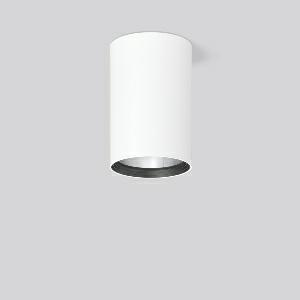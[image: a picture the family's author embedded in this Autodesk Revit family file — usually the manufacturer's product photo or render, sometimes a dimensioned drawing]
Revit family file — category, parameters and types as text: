
# Revit family: heledon_maxi_a_931223_002_1_76_c0e3
name_source: partatom
category: Lighting Fixtures
units: mm (PartAtom-declared; Revit-internal decimal feet)

## family parameters
Cut with Voids When Loaded = No
Host = Face
Light Source = No
Part Type = Normal
Room Calculation Point = No
Round Connector Dimension = Use Diameter
Shared = No

## types (1)
- HELEDON maxi A (1 x LED Modul 940, 4400 lm, 4000)
    Apparent Load = 35 VA
    Approval mark = CE
    CIE Flux Codes = 100 100 100 100 100
    Color Rendering = 92
    Color Temperature = 4000
    Default Elevation = 1800 mm
    Description = Series: HELEDON maxi
Cylindrical surface-mounted downlight. Housing: die-cast aluminium, powder-coated. Internal ceiling frame polycarbonate with bayonet mounting. Black plastic ring and recessed LED to prevent glare from the side. Optical assembly with reflector made of MIRO-Silver with 98% total light reflection for outstanding efficiency - can be changed without tools. Best colour rendering index Ra>90. Suitable for Ceiling mounting. Easy installation with a separate ceiling frame with bayonet mounting and plug connection. Driver integrated. Connected via plug-in connector. High quality converter without flickering and stroboscopic effect. The following accessories can be mounted without use of tools: interchangeable lenses, decorative glasses, honeycomb louvre, clear and frosted diffusers, white interchangeable plastic ring. 
Colour: traffic white, matt (RAL 9016)
Diameter: 123 mm
Height: 183 mm
Lamp: LED
Socket: without socket
Colour temperature: 4000K
Colour rendering index (CRI): 92
System power: 35 W
Rated luminous flux: 4400 lm
Luminous efficiency: 126 lm/W
Control gear: Converter, dimmable, DALI
Protection class: I
Type of protection: IP 20
    Height = 183 mm
    Lamp = 1 x LED Modul 940
    Lamp Light Flux = 4400 lm
    Lamp count = 1
    Length = 123 mm
    Lifetime = 50000 h
    Luminous efficacy = 126 lm/W
    Manufacturer = RZB
    ModVariant = No
    Model = 931223.002.1.76
    Mounting Place = Ceiling
    Mounting Type = Surface mounted
    Number of Poles = 1
    OnlyDefault = Yes
    Power Factor = 1
    Product Name = HELEDON maxi A
    Product group = Surface mounted downlights
    ProductGroupID = 302
    Protection Class = Protection class I
    Protection Degree = IP 20
    RLX_Detail_Level = 1
    RLX_Emergency_Light_Flux = 0 lm
    RLX_Emergency_Type = 0
    RLX_Emergency_Type_DB = No
    RlxData = <blob elided: 99901 chars, md5=88c22183>
    Socket = socket
    Standby Power = 0 W
    System Light Flux = 4400 lm
    System Power = 35 W
    Type Comments = Product without accessories
    Type Image = 931192.002.jpg
    URL = http://relux.com
    VarID = ---
    Voltage = 230 V
    Voltage Range = 220-240 V
    Weight = 0.00 kg
    Width = 0 mm  [stored 0 ft]

note: [stored X ft] marks values corroborated as IEEE doubles in the binary element streams (Revit-internal decimal feet)

## geometry (parser evidence)
native form markers: Blend x4, Sweep x10
no freeform markers — native parametric forms only
